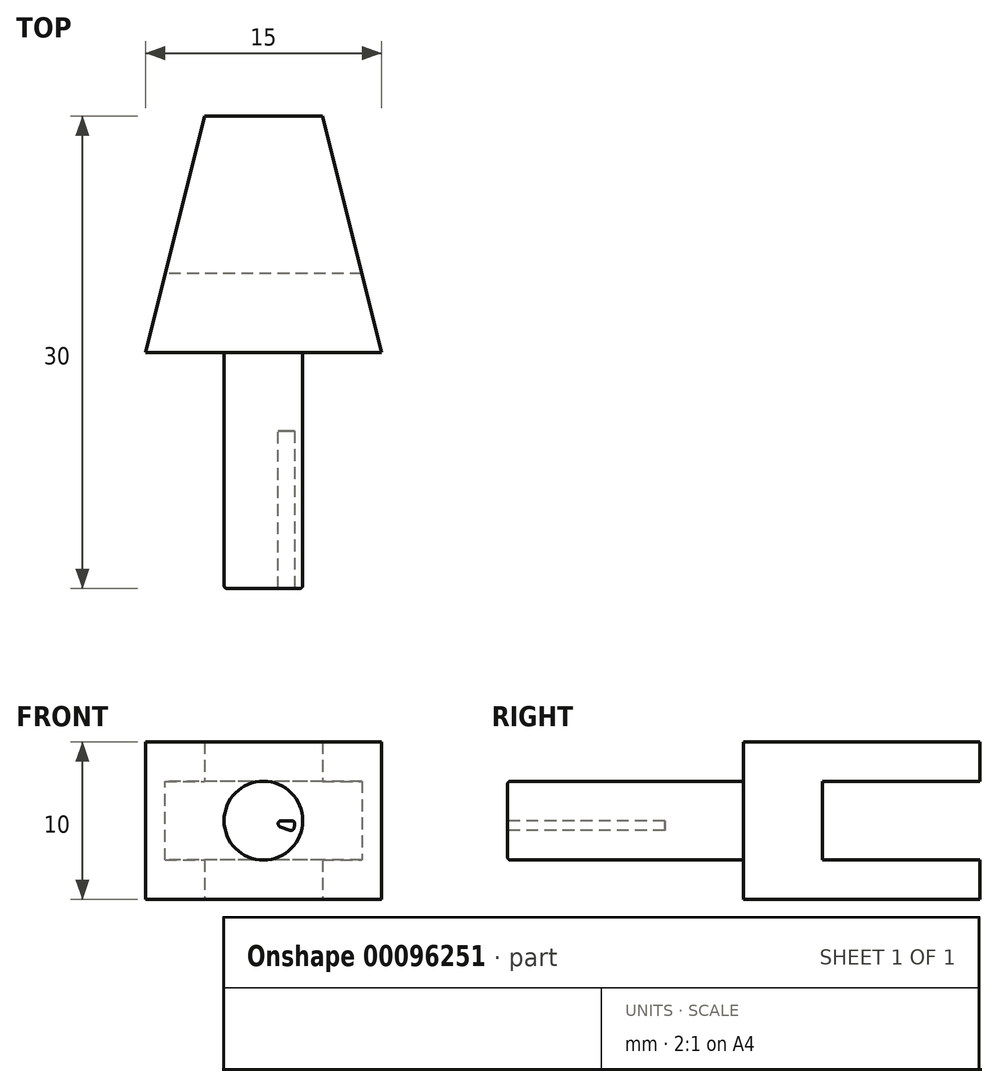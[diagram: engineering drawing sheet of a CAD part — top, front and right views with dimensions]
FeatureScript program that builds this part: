
annotation { "Feature Type Name" : "Feature", "Feature Type Description" : "" }
export const myFeature = defineFeature(function(context is Context, id is Id, definition is map)
    precondition{}
    {
        {
            var Q0;
            Q0=qCreatedBy(makeId("Top.planeOp"),FACE);
            var sketch = newSketch(context, id + "F0", { "sketchPlane" : qUnion([Q0])});
            skLineSegment(sketch, "E0.bottom", {"start": v(7.5, -7.5) * mm, "end": v(-7.5, -7.5) * mm});
            skLineSegment(sketch, "E0.top", {"start": v(7.5, 7.5) * mm, "end": v(-7.5, 7.5) * mm});
            skLineSegment(sketch, "E0.left", {"start": v(7.5, -7.5) * mm, "end": v(7.5, 7.5) * mm});
            skLineSegment(sketch, "E0.right", {"start": v(-7.5, -7.5) * mm, "end": v(-7.5, 7.5) * mm});
            skPoint(sketch, "E0.middle", {"position": v(0, 0) * mm});
            skLineSegment(sketch, "E1", {"start": v(0, 22.5) * mm, "end": v(0, -7.5) * mm, "construction": true});
            skLineSegment(sketch, "E2", {"start": v(-7.5, -7.5) * mm, "end": v(0, 22.5) * mm});
            skLineSegment(sketch, "E3", {"start": v(0, 22.5) * mm, "end": v(7.5, -7.5) * mm});
            skSolve(sketch);
        }
        {
            var Q0;
            {var subQ0=sQuery(id+"F0.wireOp",EDGE,"E0.bottom");Q0=makeQuery(id+"F0.imprint","IMPRINT",FACE,{"disambiguationData":[TD([[makeQuery(id+"F0.imprint","IMPRINT",EDGE,{"derivedFrom":subQ0}),-1.0]])]});}
            extrude(context, id + "F1", {"entities" : qUnion([Q0]), "depth" : 10 * mm});
        }
        {
            var Q0;
            Q0=qCreatedBy(makeId("Right.planeOp"),FACE);
            var sketch = newSketch(context, id + "F2", { "sketchPlane" : qUnion([Q0])});
            skLineSegment(sketch, "E4", {"start": v(-30.48, 5) * mm, "end": v(31.72, 5) * mm, "construction": true});
            skLineSegment(sketch, "E5", {"start": v(-2.5, 5) * mm, "end": v(-2.5, 7.5) * mm});
            skLineSegment(sketch, "E6", {"start": v(-2.5, 7.5) * mm, "end": v(16.89, 7.5) * mm});
            skLineSegment(sketch, "E7", {"start": v(16.89, 7.5) * mm, "end": v(16.89, 5) * mm});
            skLineSegment(sketch, "E8.MirrorCS", {"start": v(16.89, 2.5) * mm, "end": v(16.89, 5) * mm});
            skLineSegment(sketch, "E9.MirrorCS", {"start": v(-2.5, 5) * mm, "end": v(-2.5, 2.5) * mm});
            skLineSegment(sketch, "E10.MirrorCS", {"start": v(-2.5, 2.5) * mm, "end": v(16.89, 2.5) * mm});
            skSolve(sketch);
        }
        {
            var Q0;
            Q0=makeQuery(id+"F2.imprint","IMPRINT",FACE,{"disambiguationData":[TD([[makeQuery(id+"F2.imprint","IMPRINT",EDGE,{"derivedFrom":sQuery(id+"F2.wireOp",EDGE,"E5")}),-1.0]])]});
            extrude(context, id + "F3", {"entities" : qUnion([Q0]), "operationType" : NewBodyOperationType.REMOVE, "endBound" : BoundingType.SYMMETRIC, "depth" : 25 * mm});
        }
        {
            var Q0;
            Q0=makeQuery(id+"F1.opExtrude","SWEPT_FACE",FACE,{"disambiguationData":[OSD([sQuery(id+"F0.wireOp",EDGE,"E0.bottom")])]});
            var sketch = newSketch(context, id + "F4", { "sketchPlane" : qUnion([Q0])});
            skCircle(sketch, "E11", {"center": v(0, 5) * mm, "radius": 5 * mm, "construction": true});
            skPoint(sketch, "E11.first.point", {"position": v(0, 0) * mm});
            skPoint(sketch, "E11.second.point", {"position": v(0, 10) * mm});
            skPoint(sketch, "E11.third.point", {"position": v(5, 5.04) * mm});
            skLineSegment(sketch, "E12", {"start": v(0, -5.19) * mm, "end": v(0, 13.69) * mm, "construction": true});
            skCircle(sketch, "E13", {"center": v(0, 5) * mm, "radius": 2.5 * mm});
            skSolve(sketch);
        }
        {
            var Q0;
            Q0 = qSketchRegion(id + "F4", true);
            extrude(context, id + "F5", {"entities" : qUnion([Q0]), "operationType" : NewBodyOperationType.ADD, "depth" : 15 * mm});
        }
        {
            var Q0;
            Q0=makeQuery(id+"F5.opExtrude","CAP_FACE",FACE,{"disambiguationData":[OSD([sQuery(id+"F4.wireOp",EDGE,"E13")])],"isStart":false});
            var sketch = newSketch(context, id + "F6", { "sketchPlane" : qUnion([Q0])});
            skLineSegment(sketch, "E14", {"start": v(2.5, 5) * mm, "end": v(0, 5) * mm});
            skLineSegment(sketch, "E15", {"start": v(0, 5) * mm, "end": v(2.35, 4.14) * mm});
            skArc(sketch, "E16", {"start": v(2, 5) * mm, "mid": v(1.97, 4.65) * mm, "end": v(1.88, 4.32) * mm});
            skSolve(sketch);
        }
        {
            var Q0;
            {var subQ3=sQuery(id+"F6.wireOp",EDGE,"E16");Q0=makeQuery(id+"F6.imprint","IMPRINT",FACE,{"disambiguationData":[TD([[makeQuery(id+"F6.imprint","IMPRINT",EDGE,{"derivedFrom":subQ3}),1.0]])]});}
            extrude(context, id + "F7", {"entities" : qUnion([Q0]), "operationType" : NewBodyOperationType.REMOVE, "oppositeDirection" : true, "depth" : 10 * mm});
        }
        {
            var Q0;
            Q0=makeQuery(id+"F7.boolean.opBoolean","COPY",EDGE,{"derivedFrom":makeQuery(id+"F7.opExtrude","SWEPT_EDGE",EDGE,{"disambiguationData":[OSD([sQuery(id+"F4.wireOp",EDGE,"E13"),sQuery(id+"F6.wireOp",EDGE,"E14")])]})});
            var Q1;
            Q1=makeQuery(id+"F7.boolean.opBoolean","COPY",EDGE,{"derivedFrom":makeQuery(id+"F7.opExtrude","SWEPT_EDGE",EDGE,{"disambiguationData":[OSD([sQuery(id+"F4.wireOp",EDGE,"E13"),sQuery(id+"F6.wireOp",EDGE,"E15")])]})});
            var Q2;
            Q2=makeQuery(id+"F5.opExtrude","CAP_EDGE",EDGE,{"disambiguationData":[OSD([sQuery(id+"F4.wireOp",EDGE,"E13")])],"isStart":false});
            fillet(context, id + "F8", {"entities" : qUnion([Q0, Q1, Q2]), "radius" : 0.2 * mm, "tangentPropagation" : true, "allowEdgeOverflow" : false});
        }
    });
